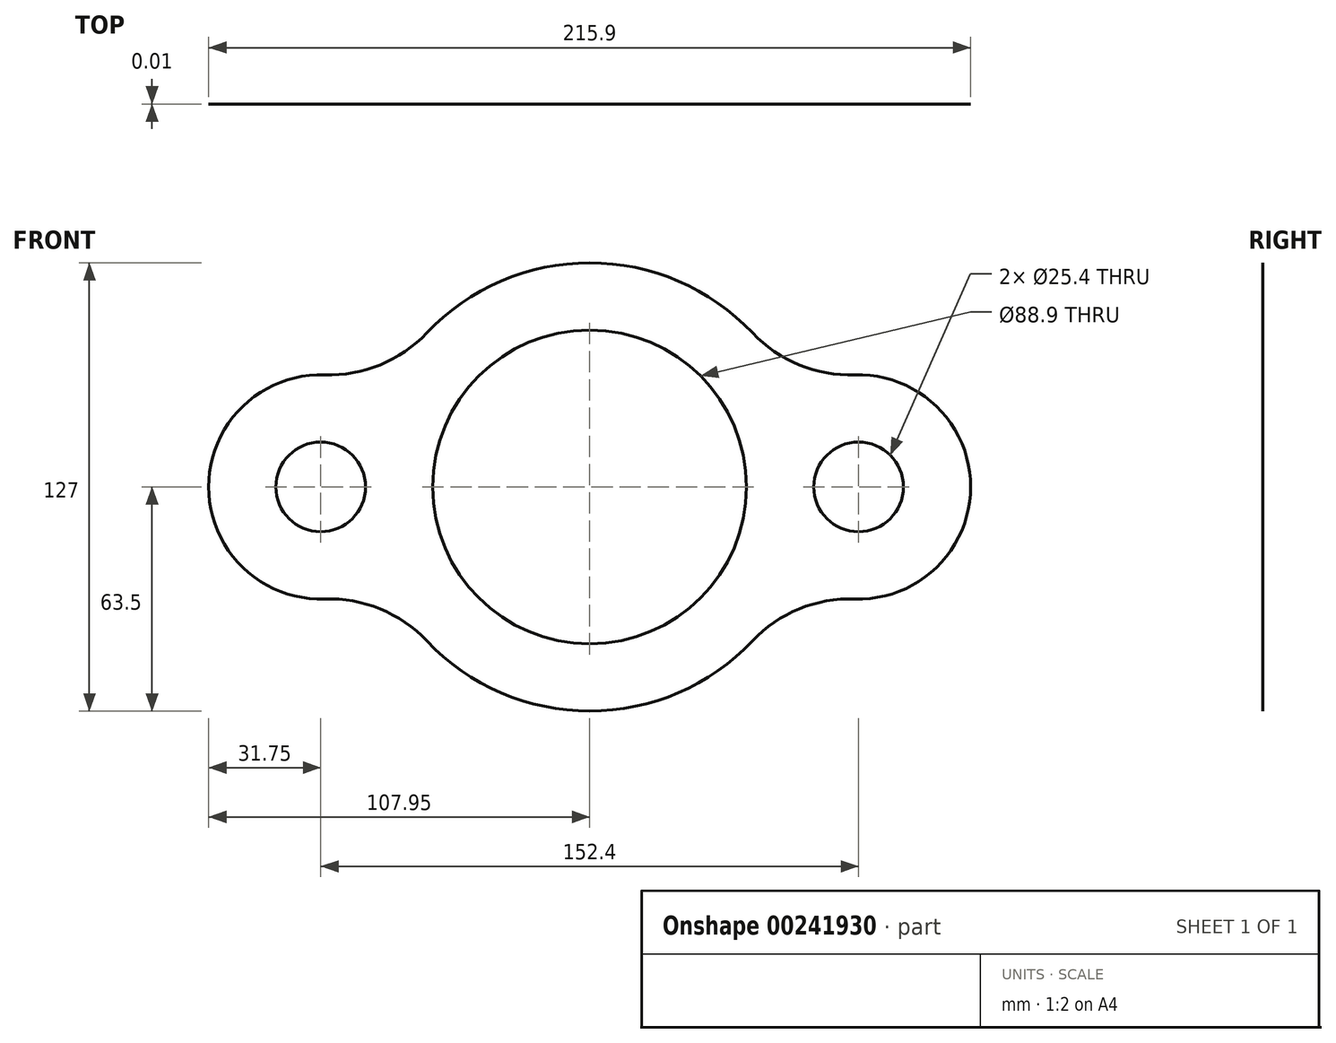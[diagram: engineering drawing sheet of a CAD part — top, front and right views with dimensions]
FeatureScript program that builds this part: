
annotation { "Feature Type Name" : "Feature", "Feature Type Description" : "" }
export const myFeature = defineFeature(function(context is Context, id is Id, definition is map)
    precondition{}
    {
        {
            var Q0;
            Q0=qCreatedBy(makeId("Front.planeOp"),FACE);
            var sketch = newSketch(context, id + "F0", { "sketchPlane" : qUnion([Q0])});
            skCircle(sketch, "E0", {"center": v(0, 0) * mm, "radius": 44.45 * mm});
            skCircle(sketch, "E1", {"center": v(-76.2, 0) * mm, "radius": 12.7 * mm});
            skCircle(sketch, "E2", {"center": v(76.2, 0) * mm, "radius": 12.7 * mm});
            skArc(sketch, "E3", {"start": v(-75.12, 31.73) * mm, "mid": v(-107.95, 0) * mm, "end": v(-75.12, -31.73) * mm});
            skArc(sketch, "E4", {"start": v(75.12, -31.73) * mm, "mid": v(107.95, 0) * mm, "end": v(75.12, 31.73) * mm});
            skArc(sketch, "E5", {"start": v(46.14, 43.63) * mm, "mid": v(0, 63.5) * mm, "end": v(-46.14, 43.63) * mm});
            skArc(sketch, "E6.trimOffspring", {"start": v(-46.14, -43.63) * mm, "mid": v(0, -63.5) * mm, "end": v(46.14, -43.63) * mm});
            skPoint(sketch, "E7.visualSharp", {"position": v(-57.94, 25.98) * mm});
            skArc(sketch, "E7.filletArc", {"start": v(-75.12, 31.73) * mm, "mid": v(-59.35, 34.56) * mm, "end": v(-46.14, 43.63) * mm});
            skPoint(sketch, "E8.visualSharp", {"position": v(-57.94, -25.98) * mm});
            skArc(sketch, "E8.filletArc", {"start": v(-46.14, -43.63) * mm, "mid": v(-59.35, -34.56) * mm, "end": v(-75.12, -31.73) * mm});
            skPoint(sketch, "E9.visualSharp", {"position": v(57.94, -25.98) * mm});
            skArc(sketch, "E9.filletArc", {"start": v(75.12, -31.73) * mm, "mid": v(59.35, -34.56) * mm, "end": v(46.14, -43.63) * mm});
            skPoint(sketch, "E10.visualSharp", {"position": v(57.94, 25.98) * mm});
            skArc(sketch, "E10.filletArc", {"start": v(46.14, 43.63) * mm, "mid": v(59.35, 34.56) * mm, "end": v(75.12, 31.73) * mm});
            skSolve(sketch);
        }
        {
            var Q0;
            Q0=makeQuery(id+"F0.imprint","IMPRINT",FACE,{"disambiguationData":[TD([[makeQuery(id+"F0.imprint","IMPRINT",EDGE,{"derivedFrom":sQuery(id+"F0.wireOp",EDGE,"E0")}),-1.0]])]});
            extrude(context, id + "F1", {"entities" : qUnion([Q0]), "depth" : 1 / 101.6 * mm});
        }
    });
